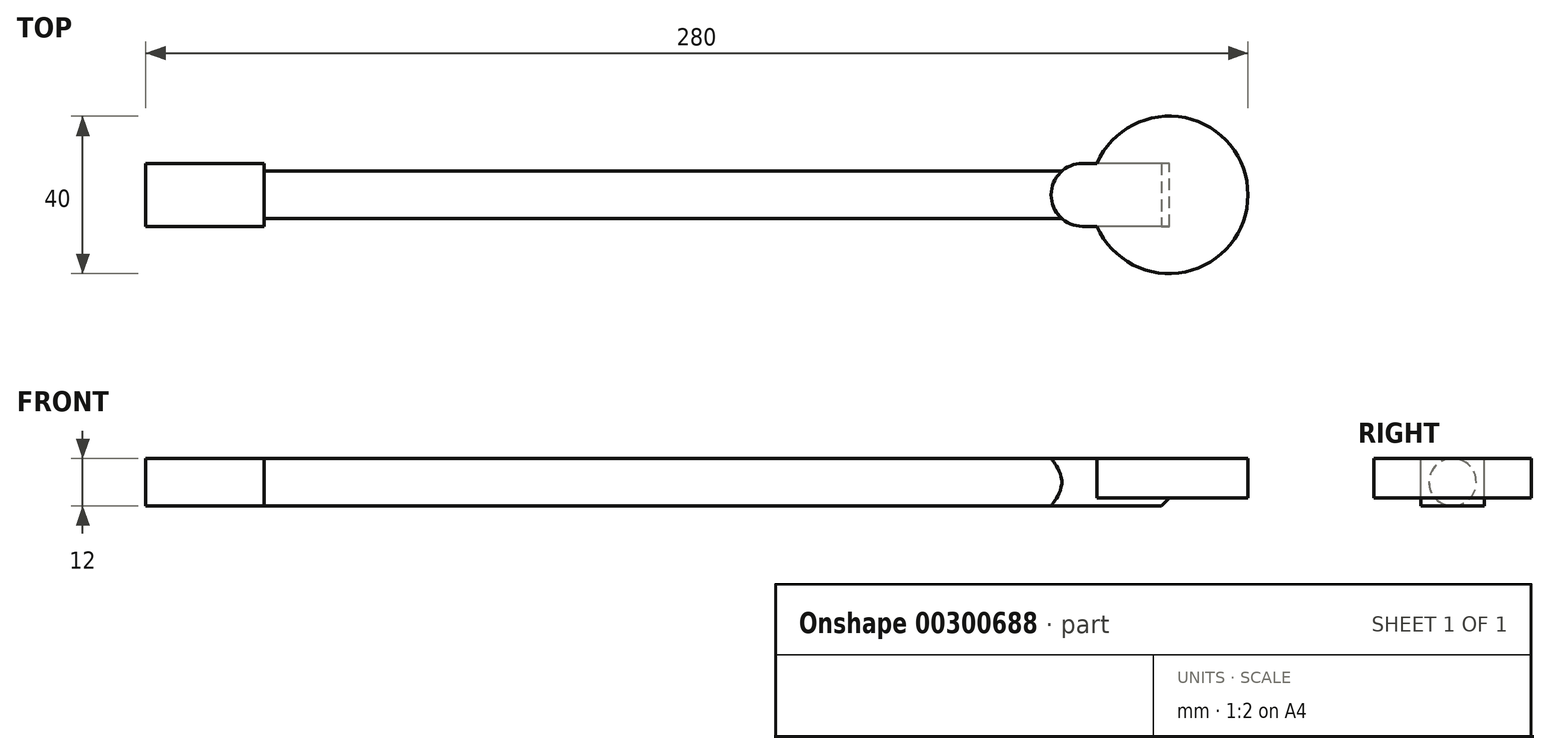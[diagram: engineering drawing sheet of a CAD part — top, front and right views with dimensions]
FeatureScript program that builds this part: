
annotation { "Feature Type Name" : "Feature", "Feature Type Description" : "" }
export const myFeature = defineFeature(function(context is Context, id is Id, definition is map)
    precondition{}
    {
        {
            var Q0;
            Q0=qCreatedBy(makeId("Front.planeOp"),FACE);
            var sketch = newSketch(context, id + "F0", { "sketchPlane" : qUnion([Q0])});
            skLineSegment(sketch, "E0.bottom", {"start": v(0, 0) * mm, "end": v(30, 0) * mm});
            skLineSegment(sketch, "E0.top", {"start": v(0, 12) * mm, "end": v(30, 12) * mm});
            skLineSegment(sketch, "E0.left", {"start": v(0, 0) * mm, "end": v(0, 12) * mm});
            skLineSegment(sketch, "E0.right", {"start": v(30, 0) * mm, "end": v(30, 12) * mm});
            skSolve(sketch);
        }
        {
            var Q0;
            Q0=makeQuery(id+"F0.imprint","IMPRINT",FACE,{"disambiguationData":[TD([[makeQuery(id+"F0.imprint","IMPRINT",EDGE,{"derivedFrom":sQuery(id+"F0.wireOp",EDGE,"E0.bottom")}),1.0]])]});
            extrude(context, id + "F1", {"entities" : qUnion([Q0]), "depth" : 16 * mm});
        }
        {
            var Q0;
            Q0=makeQuery(id+"F1.opExtrude","SWEPT_FACE",FACE,{"disambiguationData":[OSD([sQuery(id+"F0.wireOp",EDGE,"E0.right")])]});
            var sketch = newSketch(context, id + "F2", { "sketchPlane" : qUnion([Q0])});
            skCircle(sketch, "E1", {"center": v(-8, 6) * mm, "radius": 6 * mm});
            skPoint(sketch, "E1.centerSnap0", {"position": v(-16, 6) * mm});
            skPoint(sketch, "E1.centerSnap1", {"position": v(-8, 0) * mm});
            skSolve(sketch);
        }
        {
            var Q0;
            {var subQ0=sQuery(id+"F2.wireOp",EDGE,"E1");var subQ1=sQuery(id+"F0.wireOp",EDGE,"E0.right");var subQ2=makeQuery(id+"F2.imprint","INTERSECT",VERTEX,{"derivedFrom":[makeQuery(id+"F1.opExtrude","SWEPT_EDGE",EDGE,{"disambiguationData":[OSD([sQuery(id+"F0.wireOp",EDGE,"E0.bottom"),subQ1])]}),subQ0]});Q0=makeQuery(id+"F2.imprint","IMPRINT",FACE,{"disambiguationData":[TD([[makeQuery(id+"F2.imprint","IMPRINT",EDGE,{"disambiguationData":[TD([[subQ2,1.0]])],"derivedFrom":subQ0}),1.0]])]});}
            extrude(context, id + "F3", {"entities" : qUnion([Q0]), "operationType" : NewBodyOperationType.ADD, "depth" : 200 * mm});
        }
        {
            var Q0;
            Q0=makeQuery(id+"F3.opExtrude","CAP_FACE",FACE,{"disambiguationData":[OSD([sQuery(id+"F2.wireOp",EDGE,"E1")])],"isStart":false});
            var sketch = newSketch(context, id + "F4", { "sketchPlane" : qUnion([Q0])});
            skPoint(sketch, "E2.middle", {"position": v(-8, 6) * mm});
            skLineSegment(sketch, "E3.bottom", {"start": v(-16, 12) * mm, "end": v(0, 12) * mm});
            skLineSegment(sketch, "E3.top", {"start": v(-16, 0) * mm, "end": v(0, 0) * mm});
            skLineSegment(sketch, "E3.left", {"start": v(-16, 12) * mm, "end": v(-16, 0) * mm});
            skLineSegment(sketch, "E3.right", {"start": v(0, 12) * mm, "end": v(0, 0) * mm});
            skSolve(sketch);
        }
        {
            var Q0;
            {var subQ0=sQuery(id+"F4.wireOp",EDGE,"E3.left");Q0=makeQuery(id+"F4.imprint","IMPRINT",FACE,{"disambiguationData":[TD([[makeQuery(id+"F4.imprint","IMPRINT",EDGE,{"derivedFrom":subQ0}),1.0]])]});}
            var Q1;
            {var subQ0=sQuery(id+"F4.wireOp",EDGE,"E3.right");Q1=makeQuery(id+"F4.imprint","IMPRINT",FACE,{"disambiguationData":[TD([[makeQuery(id+"F4.imprint","IMPRINT",EDGE,{"derivedFrom":subQ0}),-1.0]])]});}
            var Q2;
            {var subQ0=makeQuery(id+"F3.opExtrude","CAP_EDGE",EDGE,{"disambiguationData":[OSD([sQuery(id+"F2.wireOp",EDGE,"E1")])],"isStart":false});var subQ1=makeQuery(id+"F4.imprint","INTERSECT",VERTEX,{"derivedFrom":[subQ0,sQuery(id+"F4.wireOp",EDGE,"E3.bottom")]});Q2=makeQuery(id+"F4.imprint","IMPRINT",FACE,{"disambiguationData":[TD([[makeQuery(id+"F4.imprint","IMPRINT",EDGE,{"disambiguationData":[TD([[subQ1,-1.0]])],"derivedFrom":subQ0}),1.0]])]});}
            extrude(context, id + "F5", {"entities" : qUnion([Q0, Q1, Q2]), "operationType" : NewBodyOperationType.ADD, "depth" : 30 * mm});
        }
        {
            var Q0;
            Q0=makeQuery(id+"F5.opExtrude","SWEPT_FACE",FACE,{"disambiguationData":[OSD([sQuery(id+"F4.wireOp",EDGE,"E3.bottom")])]});
            var sketch = newSketch(context, id + "F6", { "sketchPlane" : qUnion([Q0])});
            skCircle(sketch, "E4", {"center": v(260, -8) * mm, "radius": 20 * mm});
            skSolve(sketch);
        }
        {
            var Q0;
            {var subQ1=sQuery(id+"F4.wireOp",EDGE,"E3.bottom");var subQ6=makeQuery(id+"F5.opExtrude","CAP_EDGE",EDGE,{"disambiguationData":[OSD([subQ1])],"isStart":false});Q0=makeQuery(id+"F6.imprint","IMPRINT",FACE,{"disambiguationData":[TD([[makeQuery(id+"F6.imprint","IMPRINT",EDGE,{"derivedFrom":subQ6}),-1.0]])]});}
            extrude(context, id + "F7", {"entities" : qUnion([Q0]), "operationType" : NewBodyOperationType.ADD, "oppositeDirection" : true, "depth" : 10 * mm});
        }
        {
            var Q0;
            Q0=makeQuery(id+"F5.opExtrude","CAP_EDGE",EDGE,{"disambiguationData":[OSD([sQuery(id+"F4.wireOp",EDGE,"E3.right")])],"isStart":true});
            var Q1;
            Q1=makeQuery(id+"F5.opExtrude","CAP_EDGE",EDGE,{"disambiguationData":[OSD([sQuery(id+"F4.wireOp",EDGE,"E3.left")])],"isStart":true});
            fillet(context, id + "F8", {"entities" : qUnion([Q0, Q1]), "radius" : 8 * mm, "tangentPropagation" : true, "allowEdgeOverflow" : false});
        }
        {
            var Q0;
            Q0=makeQuery(id+"F5.opExtrude","CAP_EDGE",EDGE,{"disambiguationData":[OSD([sQuery(id+"F4.wireOp",EDGE,"E3.top")])],"isStart":false});
            chamfer(context, id + "F9", {"entities" : qUnion([Q0]), "width" : 2 * mm, "tangentPropagation" : true});
        }
    });
